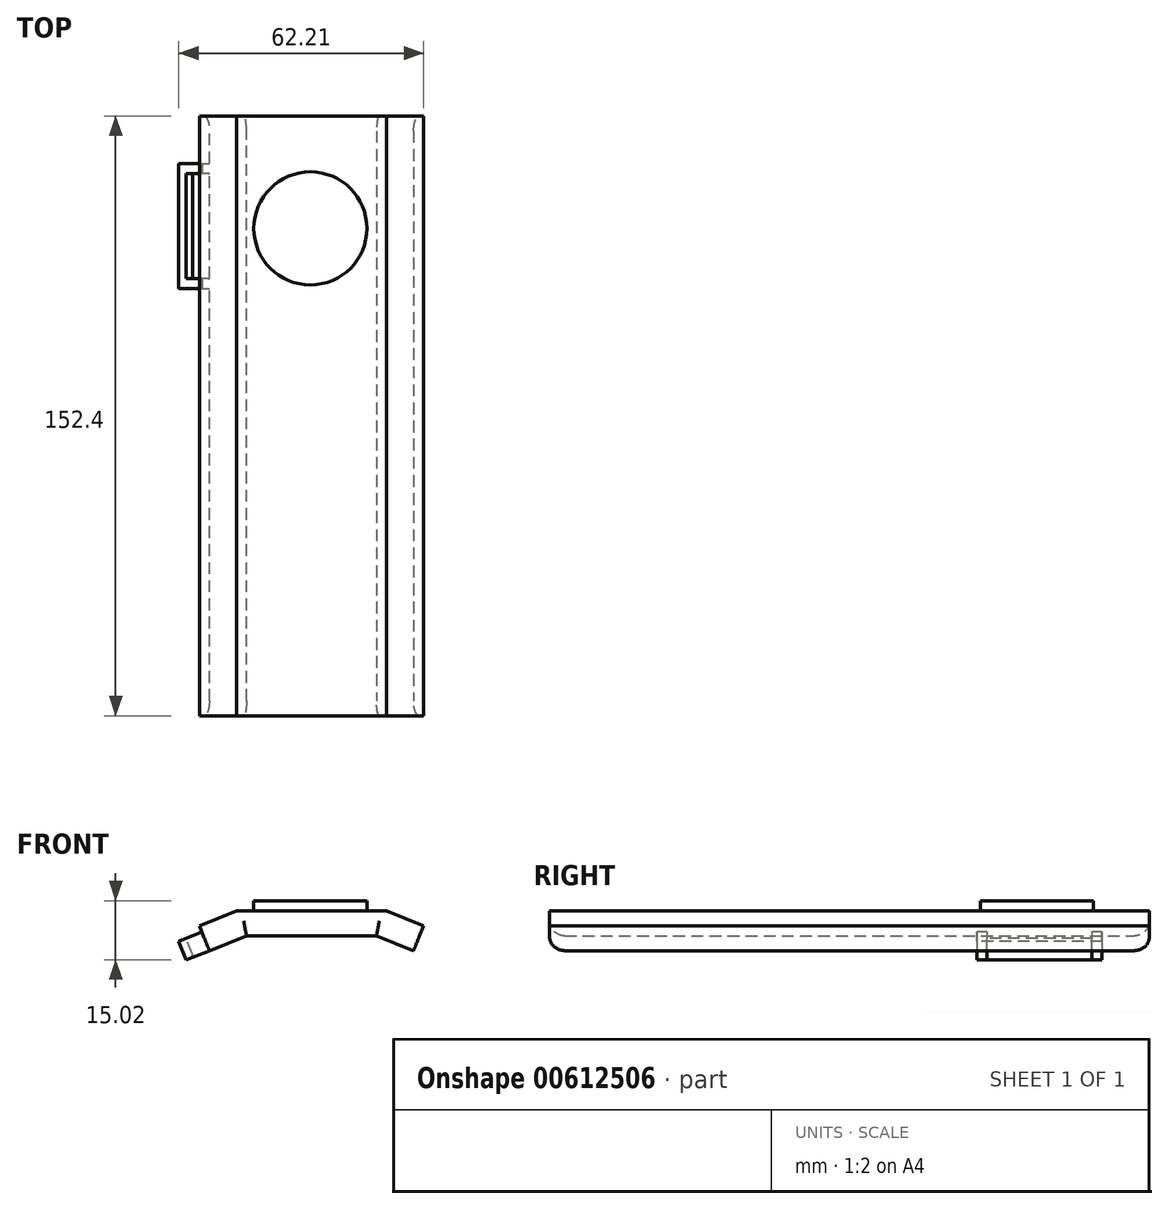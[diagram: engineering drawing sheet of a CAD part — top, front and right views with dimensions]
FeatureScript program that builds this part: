
annotation { "Feature Type Name" : "Feature", "Feature Type Description" : "" }
export const myFeature = defineFeature(function(context is Context, id is Id, definition is map)
    precondition{}
    {
        {
            var Q0;
            Q0=qCreatedBy(makeId("Top.planeOp"),FACE);
            var sketch = newSketch(context, id + "F0", { "sketchPlane" : qUnion([Q0])});
            skLineSegment(sketch, "E0.bottom", {"start": v(-18.76, 115.88) * mm, "end": v(19.34, 115.88) * mm});
            skLineSegment(sketch, "E0.top", {"start": v(-18.76, -36.52) * mm, "end": v(19.34, -36.52) * mm});
            skLineSegment(sketch, "E0.left", {"start": v(-18.76, 115.88) * mm, "end": v(-18.76, -36.52) * mm});
            skLineSegment(sketch, "E0.right", {"start": v(19.34, 115.88) * mm, "end": v(19.34, -36.52) * mm});
            skSolve(sketch);
        }
        {
            var Q0;
            Q0=makeQuery(id+"F0.imprint","IMPRINT",FACE,{"disambiguationData":[TD([[makeQuery(id+"F0.imprint","IMPRINT",EDGE,{"derivedFrom":sQuery(id+"F0.wireOp",EDGE,"E0.bottom")}),-1.0]])]});
            extrude(context, id + "F1", {"entities" : qUnion([Q0]), "depth" : 6.35 * mm, "offsetDistance" : 25.4 * mm});
        }
        {
            var Q0;
            Q0=makeQuery(id+"F1.opExtrude","CAP_EDGE",EDGE,{"disambiguationData":[OSD([sQuery(id+"F0.wireOp",EDGE,"E0.left")])],"isStart":true});
            var Q1;
            Q1=makeQuery(id+"F1.opExtrude","CAP_EDGE",EDGE,{"disambiguationData":[OSD([sQuery(id+"F0.wireOp",EDGE,"E0.right")])],"isStart":true});
            chamfer(context, id + "F2", {"entities" : qUnion([Q0, Q1]), "chamferType" : ChamferType.TWO_OFFSETS, "width1" : 6.35 * mm, "oppositeDirection" : false, "width2" : 2.54 * mm, "tangentPropagation" : true});
        }
        {
            var Q0;
            Q0=makeQuery(id+"F2.opChamfer","BLEND_FACE",FACE,{"disambiguationData":[OSD([sQuery(id+"F0.wireOp",EDGE,"E0.left")])]});
            var sketch = newSketch(context, id + "F3", { "sketchPlane" : qUnion([Q0])});
            skLineSegment(sketch, "E1.bottom", {"start": v(-115.88, 12.86) * mm, "end": v(36.52, 12.86) * mm});
            skLineSegment(sketch, "E1.top", {"start": v(-115.88, 6.03) * mm, "end": v(36.52, 6.03) * mm});
            skLineSegment(sketch, "E1.left", {"start": v(-115.88, 12.86) * mm, "end": v(-115.88, 6.03) * mm});
            skLineSegment(sketch, "E1.right", {"start": v(36.52, 12.86) * mm, "end": v(36.52, 6.03) * mm});
            skSolve(sketch);
        }
        {
            var Q0;
            Q0=makeQuery(id+"F3.imprint","IMPRINT",FACE,{"disambiguationData":[TD([[makeQuery(id+"F3.imprint","IMPRINT",EDGE,{"derivedFrom":sQuery(id+"F3.wireOp",EDGE,"E1.bottom")}),-1.0]])]});
            extrude(context, id + "F4", {"entities" : qUnion([Q0]), "operationType" : NewBodyOperationType.ADD, "depth" : 10.16 * mm, "offsetDistance" : 25.4 * mm});
        }
        {
            var Q0;
            Q0=makeQuery(id+"F2.opChamfer","BLEND_FACE",FACE,{"disambiguationData":[OSD([sQuery(id+"F0.wireOp",EDGE,"E0.right")])]});
            var sketch = newSketch(context, id + "F5", { "sketchPlane" : qUnion([Q0])});
            skLineSegment(sketch, "E2.bottom", {"start": v(-36.52, 13.08) * mm, "end": v(115.88, 13.08) * mm});
            skLineSegment(sketch, "E2.top", {"start": v(-36.52, 6.24) * mm, "end": v(115.88, 6.24) * mm});
            skLineSegment(sketch, "E2.left", {"start": v(-36.52, 13.08) * mm, "end": v(-36.52, 6.24) * mm});
            skLineSegment(sketch, "E2.right", {"start": v(115.88, 13.08) * mm, "end": v(115.88, 6.24) * mm});
            skSolve(sketch);
        }
        {
            var Q0;
            Q0=makeQuery(id+"F5.imprint","IMPRINT",FACE,{"disambiguationData":[TD([[makeQuery(id+"F5.imprint","IMPRINT",EDGE,{"derivedFrom":sQuery(id+"F5.wireOp",EDGE,"E2.bottom")}),1.0]])]});
            extrude(context, id + "F6", {"entities" : qUnion([Q0]), "operationType" : NewBodyOperationType.ADD, "depth" : 10.16 * mm, "offsetDistance" : 25.4 * mm});
        }
        {
            var Q0;
            Q0=makeQuery(id+"F1.opExtrude","CAP_EDGE",EDGE,{"disambiguationData":[OSD([sQuery(id+"F0.wireOp",EDGE,"E0.top")])],"isStart":true});
            var Q1;
            Q1=makeQuery(id+"F4.opExtrude","SWEPT_EDGE",EDGE,{"disambiguationData":[OSD([sQuery(id+"F3.wireOp",EDGE,"E1.top"),sQuery(id+"F3.wireOp",EDGE,"E1.right")])]});
            var Q2;
            Q2=makeQuery(id+"F6.opExtrude","SWEPT_EDGE",EDGE,{"disambiguationData":[OSD([sQuery(id+"F5.wireOp",EDGE,"E2.top"),sQuery(id+"F5.wireOp",EDGE,"E2.left")])]});
            var Q3;
            Q3=makeQuery(id+"F6.opExtrude","SWEPT_EDGE",EDGE,{"disambiguationData":[OSD([sQuery(id+"F5.wireOp",EDGE,"E2.top"),sQuery(id+"F5.wireOp",EDGE,"E2.right")])]});
            var Q4;
            Q4=makeQuery(id+"F1.opExtrude","CAP_EDGE",EDGE,{"disambiguationData":[OSD([sQuery(id+"F0.wireOp",EDGE,"E0.bottom")])],"isStart":true});
            var Q5;
            Q5=makeQuery(id+"F4.opExtrude","SWEPT_EDGE",EDGE,{"disambiguationData":[OSD([sQuery(id+"F3.wireOp",EDGE,"E1.top"),sQuery(id+"F3.wireOp",EDGE,"E1.left")])]});
            fillet(context, id + "F7", {"entities" : qUnion([Q0, Q1, Q2, Q3, Q4, Q5]), "radius" : 3.8 * mm, "tangentPropagation" : true, "allowEdgeOverflow" : false});
        }
        {
            var Q0;
            Q0=makeQuery(id+"F4.opExtrude","CAP_FACE",FACE,{"disambiguationData":[OSD([sQuery(id+"F3.wireOp",EDGE,"E1.bottom"),sQuery(id+"F3.wireOp",EDGE,"E1.top"),sQuery(id+"F3.wireOp",EDGE,"E1.left"),sQuery(id+"F3.wireOp",EDGE,"E1.right")])],"isStart":false});
            var sketch = newSketch(context, id + "F8", { "sketchPlane" : qUnion([Q0])});
            skLineSegment(sketch, "E3.bottom", {"start": v(-103.83, 11.1) * mm, "end": v(-72.08, 11.1) * mm});
            skLineSegment(sketch, "E3.top", {"start": v(-103.83, 6.03) * mm, "end": v(-72.08, 6.03) * mm});
            skLineSegment(sketch, "E3.left", {"start": v(-103.83, 11.1) * mm, "end": v(-103.83, 6.03) * mm});
            skLineSegment(sketch, "E3.right", {"start": v(-72.08, 11.1) * mm, "end": v(-72.08, 6.03) * mm});
            skSolve(sketch);
        }
        {
            var Q0;
            Q0=makeQuery(id+"F8.imprint","IMPRINT",FACE,{"disambiguationData":[TD([[makeQuery(id+"F8.imprint","IMPRINT",EDGE,{"derivedFrom":sQuery(id+"F8.wireOp",EDGE,"E3.bottom")}),-1.0]])]});
            extrude(context, id + "F9", {"entities" : qUnion([Q0]), "operationType" : NewBodyOperationType.ADD, "depth" : 6.35 * mm, "offsetDistance" : 25.4 * mm});
        }
        {
            var Q0;
            Q0=makeQuery(id+"F9.opExtrude","SWEPT_FACE",FACE,{"disambiguationData":[OSD([sQuery(id+"F8.wireOp",EDGE,"E3.bottom")])]});
            var sketch = newSketch(context, id + "F10", { "sketchPlane" : qUnion([Q0])});
            skLineSegment(sketch, "E4.bottom", {"start": v(-25.22, 101.3) * mm, "end": v(-29.54, 101.3) * mm});
            skLineSegment(sketch, "E4.top", {"start": v(-25.22, 74.62) * mm, "end": v(-29.54, 74.62) * mm});
            skLineSegment(sketch, "E4.left", {"start": v(-25.22, 101.3) * mm, "end": v(-25.22, 74.62) * mm});
            skLineSegment(sketch, "E4.right", {"start": v(-29.54, 101.3) * mm, "end": v(-29.54, 74.62) * mm});
            skSolve(sketch);
        }
        {
            var Q0;
            Q0=makeQuery(id+"F10.imprint","IMPRINT",FACE,{"disambiguationData":[TD([[makeQuery(id+"F10.imprint","IMPRINT",EDGE,{"derivedFrom":sQuery(id+"F10.wireOp",EDGE,"E4.bottom")}),1.0]])]});
            extrude(context, id + "F11", {"entities" : qUnion([Q0]), "operationType" : NewBodyOperationType.REMOVE, "oppositeDirection" : true, "depth" : 25.4 * mm, "offsetDistance" : 25.4 * mm});
        }
        {
            var Q0;
            Q0=makeQuery(id+"F11.boolean.opBoolean","COPY",EDGE,{"derivedFrom":makeQuery(id+"F11.opExtrude","CAP_EDGE",EDGE,{"disambiguationData":[OSD([sQuery(id+"F10.wireOp",EDGE,"E4.right")])],"isStart":true})});
            var Q1;
            Q1=makeQuery(id+"F11.boolean.opBoolean","INTERSECT",EDGE,{"derivedFrom":[makeQuery(id+"F9.boolean.opBoolean","MERGE",FACE,{"derivedFrom":[makeQuery(id+"F4.opExtrude","SWEPT_FACE",FACE,{"disambiguationData":[OSD([sQuery(id+"F3.wireOp",EDGE,"E1.top")])]}),makeQuery(id+"F9.opExtrude","SWEPT_FACE",FACE,{"disambiguationData":[OSD([sQuery(id+"F8.wireOp",EDGE,"E3.top")])]})]}),makeQuery(id+"F11.opExtrude","SWEPT_FACE",FACE,{"disambiguationData":[OSD([sQuery(id+"F10.wireOp",EDGE,"E4.right")])]})]});
            fillet(context, id + "F12", {"entities" : qUnion([Q0, Q1]), "radius" : 1.02 * mm, "tangentPropagation" : true, "allowEdgeOverflow" : false});
        }
        {
            var Q0;
            Q0=makeQuery(id+"F1.opExtrude","CAP_FACE",FACE,{"disambiguationData":[OSD([sQuery(id+"F0.wireOp",EDGE,"E0.bottom"),sQuery(id+"F0.wireOp",EDGE,"E0.top"),sQuery(id+"F0.wireOp",EDGE,"E0.left"),sQuery(id+"F0.wireOp",EDGE,"E0.right")])],"isStart":false});
            var sketch = newSketch(context, id + "F13", { "sketchPlane" : qUnion([Q0])});
            skCircle(sketch, "E5", {"center": v(0, 87.32) * mm, "radius": 14.37 * mm});
            skSolve(sketch);
        }
        {
            var Q0;
            Q0 = qSketchRegion(id + "F13", true);
            extrude(context, id + "F14", {"entities" : qUnion([Q0]), "operationType" : NewBodyOperationType.ADD, "depth" : 2.54 * mm, "offsetDistance" : 25.4 * mm});
        }
    });
